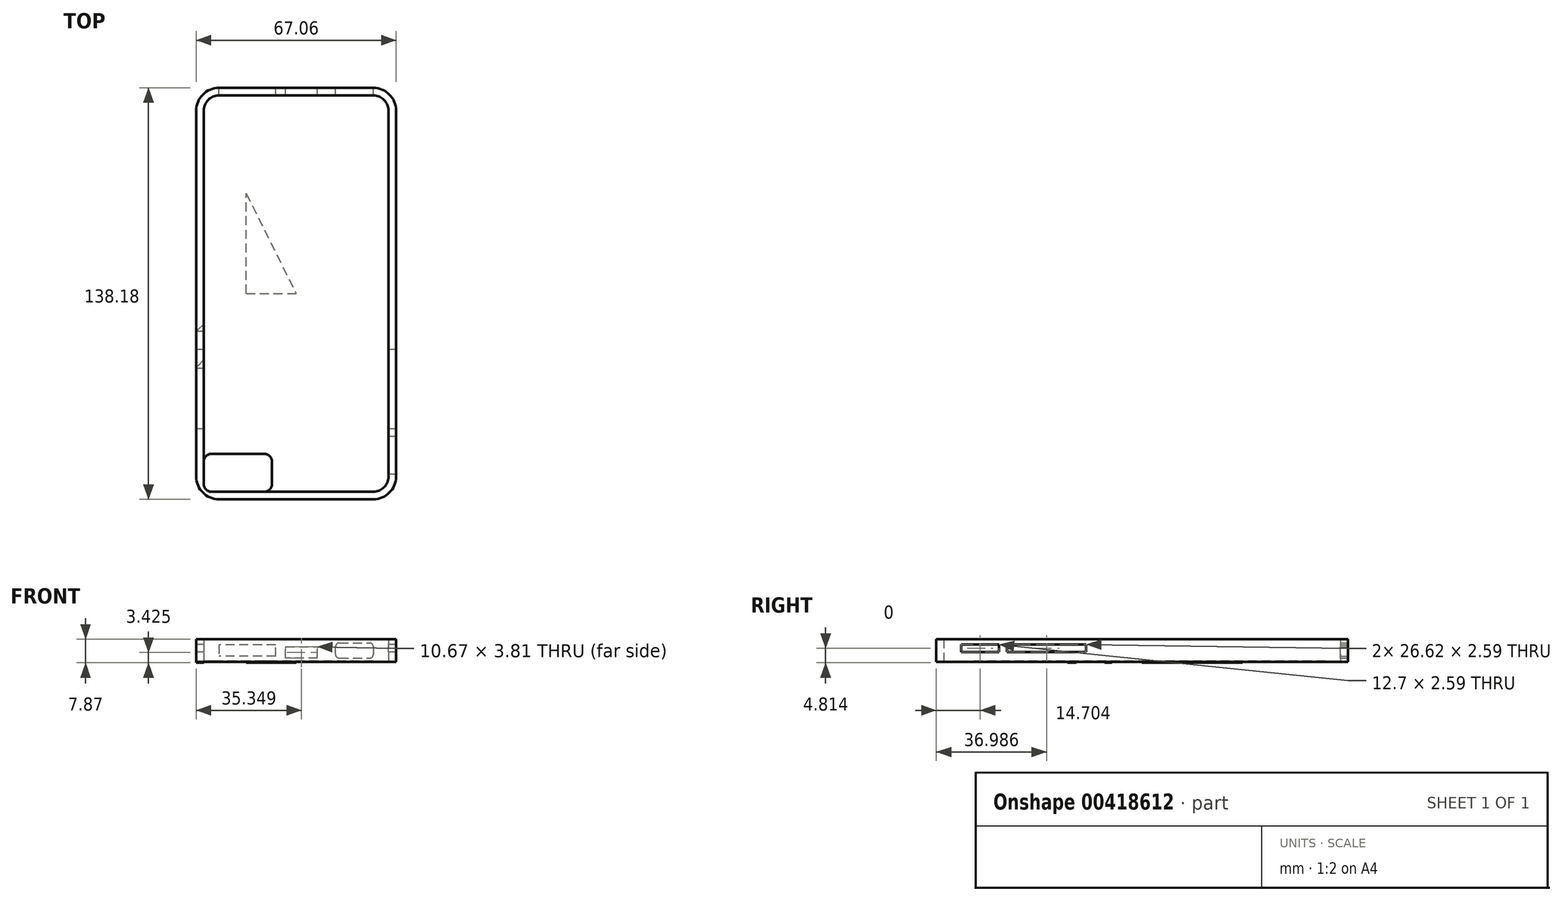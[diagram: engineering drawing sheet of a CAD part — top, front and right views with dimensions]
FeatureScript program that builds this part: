
annotation { "Feature Type Name" : "Feature", "Feature Type Description" : "" }
export const myFeature = defineFeature(function(context is Context, id is Id, definition is map)
    precondition{}
    {
        {
            var Q0;
            Q0=qCreatedBy(makeId("Top.planeOp"),FACE);
            var sketch = newSketch(context, id + "F0", { "sketchPlane" : qUnion([Q0])});
            skLineSegment(sketch, "E0", {"start": v(0, 0) * mm, "end": v(-33.53, 0) * mm});
            skLineSegment(sketch, "E1", {"start": v(-33.53, 0) * mm, "end": v(-33.53, 138.18) * mm});
            skLineSegment(sketch, "E2", {"start": v(-33.53, 138.18) * mm, "end": v(0, 138.18) * mm});
            skLineSegment(sketch, "E3", {"start": v(0, 138.18) * mm, "end": v(33.53, 138.18) * mm});
            skLineSegment(sketch, "E4", {"start": v(33.53, 138.18) * mm, "end": v(33.53, 0) * mm});
            skLineSegment(sketch, "E5", {"start": v(33.53, 0) * mm, "end": v(0, 0) * mm});
            skLineSegment(sketch, "E6", {"start": v(-30.99, 135.64) * mm, "end": v(-30.99, 2.54) * mm});
            skLineSegment(sketch, "E7", {"start": v(-30.99, 2.54) * mm, "end": v(30.99, 2.54) * mm});
            skLineSegment(sketch, "E8", {"start": v(30.99, 2.54) * mm, "end": v(30.99, 135.64) * mm});
            skLineSegment(sketch, "E9", {"start": v(30.99, 135.64) * mm, "end": v(-30.99, 135.64) * mm});
            skSolve(sketch);
        }
        {
            var Q0;
            Q0 = qSketchRegion(id + "F0", true);
            extrude(context, id + "F1", {"entities" : qUnion([Q0]), "depth" : 7.62 * mm});
        }
        {
            var Q0;
            Q0=makeQuery(id+"F0.imprint","IMPRINT",FACE,{"disambiguationData":[TD([[makeQuery(id+"F0.imprint","IMPRINT",EDGE,{"derivedFrom":sQuery(id+"F0.wireOp",EDGE,"E6")}),1.0]])]});
            extrude(context, id + "F2", {"entities" : qUnion([Q0]), "operationType" : NewBodyOperationType.ADD, "depth" : 0.25 * mm});
        }
        {
            var Q0;
            Q0=makeQuery(id+"F1.opExtrude","SWEPT_EDGE",EDGE,{"disambiguationData":[OSD([sQuery(id+"F0.wireOp",EDGE,"E0"),sQuery(id+"F0.wireOp",EDGE,"E1")])]});
            var Q1;
            Q1=makeQuery(id+"F1.opExtrude","SWEPT_EDGE",EDGE,{"disambiguationData":[OSD([sQuery(id+"F0.wireOp",EDGE,"E4"),sQuery(id+"F0.wireOp",EDGE,"E5")])]});
            var Q2;
            Q2=makeQuery(id+"F1.opExtrude","SWEPT_EDGE",EDGE,{"disambiguationData":[OSD([sQuery(id+"F0.wireOp",EDGE,"E3"),sQuery(id+"F0.wireOp",EDGE,"E4")])]});
            var Q3;
            Q3=makeQuery(id+"F1.opExtrude","SWEPT_EDGE",EDGE,{"disambiguationData":[OSD([sQuery(id+"F0.wireOp",EDGE,"E1"),sQuery(id+"F0.wireOp",EDGE,"E2")])]});
            fillet(context, id + "F3", {"entities" : qUnion([Q0, Q1, Q2, Q3]), "radius" : 7.62 * mm, "tangentPropagation" : true, "allowEdgeOverflow" : false});
        }
        {
            var Q0;
            Q0=makeQuery(id+"F1.opExtrude","SWEPT_EDGE",EDGE,{"disambiguationData":[OSD([sQuery(id+"F0.wireOp",EDGE,"E6"),sQuery(id+"F0.wireOp",EDGE,"E9")])]});
            var Q1;
            Q1=makeQuery(id+"F1.opExtrude","SWEPT_EDGE",EDGE,{"disambiguationData":[OSD([sQuery(id+"F0.wireOp",EDGE,"E8"),sQuery(id+"F0.wireOp",EDGE,"E9")])]});
            var Q2;
            Q2=makeQuery(id+"F1.opExtrude","SWEPT_EDGE",EDGE,{"disambiguationData":[OSD([sQuery(id+"F0.wireOp",EDGE,"E6"),sQuery(id+"F0.wireOp",EDGE,"E7")])]});
            var Q3;
            Q3=makeQuery(id+"F1.opExtrude","SWEPT_EDGE",EDGE,{"disambiguationData":[OSD([sQuery(id+"F0.wireOp",EDGE,"E7"),sQuery(id+"F0.wireOp",EDGE,"E8")])]});
            fillet(context, id + "F4", {"entities" : qUnion([Q0, Q1, Q2, Q3]), "radius" : 5.08 * mm, "tangentPropagation" : true, "allowEdgeOverflow" : false});
        }
        {
            var Q0;
            Q0=makeQuery(id+"F0.imprint","IMPRINT",FACE,{"disambiguationData":[TD([[makeQuery(id+"F0.imprint","IMPRINT",EDGE,{"derivedFrom":sQuery(id+"F0.wireOp",EDGE,"E6")}),1.0]])]});
            var sketch = newSketch(context, id + "F5", { "sketchPlane" : qUnion([Q0])});
            skLineSegment(sketch, "E10.0", {"start": v(-33.53, 138.18) * mm, "end": v(0, 138.18) * mm});
            skLineSegment(sketch, "E11.0", {"start": v(-33.53, 0) * mm, "end": v(-33.53, 138.18) * mm});
            skLineSegment(sketch, "E12.0", {"start": v(33.53, 138.18) * mm, "end": v(33.53, 0) * mm});
            skLineSegment(sketch, "E13.0", {"start": v(0, 0) * mm, "end": v(-33.53, 0) * mm});
            skLineSegment(sketch, "E14.0", {"start": v(33.53, 0) * mm, "end": v(0, 0) * mm});
            skPoint(sketch, "E15.start.orphan", {"position": v(-16.76, 138.18) * mm});
            skLineSegment(sketch, "E16", {"start": v(0, 138.18) * mm, "end": v(0, 69.09) * mm});
            skPoint(sketch, "E17.orphan", {"position": v(-33.53, 69.09) * mm});
            skPoint(sketch, "E18.end.orphan", {"position": v(33.53, 69.09) * mm});
            skLineSegment(sketch, "E19", {"start": v(-33.53, 69.09) * mm, "end": v(0, 69.09) * mm});
            skLineSegment(sketch, "E20", {"start": v(0, 69.09) * mm, "end": v(33.53, 69.09) * mm});
            skPoint(sketch, "E21", {"position": v(-16.76, 69.09) * mm});
            skLineSegment(sketch, "E22", {"start": v(-16.76, 69.09) * mm, "end": v(-16.76, 102.75) * mm});
            skLineSegment(sketch, "E23", {"start": v(-16.76, 102.75) * mm, "end": v(0, 69.09) * mm});
            skLineSegment(sketch, "E24", {"start": v(0, 69.09) * mm, "end": v(16.76, 69.09) * mm});
            skLineSegment(sketch, "E25", {"start": v(16.76, 69.09) * mm, "end": v(24.75, 61.14) * mm});
            skLineSegment(sketch, "E26", {"start": v(24.75, 61.14) * mm, "end": v(0, 61.14) * mm});
            skLineSegment(sketch, "E27", {"start": v(0, 61.14) * mm, "end": v(0, 52.13) * mm});
            skLineSegment(sketch, "E28", {"start": v(0, 52.13) * mm, "end": v(26.95, 52.13) * mm});
            skLineSegment(sketch, "E29", {"start": v(26.95, 52.13) * mm, "end": v(33.53, 44.08) * mm});
            skLineSegment(sketch, "E30", {"start": v(33.53, 44.08) * mm, "end": v(0, 44.08) * mm});
            skLineSegment(sketch, "E31", {"start": v(-16.76, 61.14) * mm, "end": v(-16.76, 69.09) * mm});
            skLineSegment(sketch, "E32", {"start": v(-16.76, 61.14) * mm, "end": v(-28.48, 61.14) * mm});
            skLineSegment(sketch, "E33", {"start": v(-28.48, 61.14) * mm, "end": v(-33.53, 56.5) * mm});
            skLineSegment(sketch, "E34", {"start": v(-33.53, 56.5) * mm, "end": v(-16.76, 56.5) * mm});
            skLineSegment(sketch, "E35", {"start": v(-16.76, 56.5) * mm, "end": v(-16.76, 52.13) * mm});
            skLineSegment(sketch, "E36", {"start": v(-16.76, 52.13) * mm, "end": v(-26.29, 52.13) * mm});
            skLineSegment(sketch, "E37", {"start": v(-26.29, 52.13) * mm, "end": v(-33.53, 44.08) * mm});
            skLineSegment(sketch, "E38", {"start": v(-33.53, 44.08) * mm, "end": v(0, 44.08) * mm});
            skSolve(sketch);
        }
        {
            var Q0;
            {var subQ14=sQuery(id+"F5.wireOp",EDGE,"E24");Q0=makeQuery(id+"F5.imprint","IMPRINT",FACE,{"disambiguationData":[TD([[makeQuery(id+"F5.imprint","IMPRINT",EDGE,{"derivedFrom":subQ14}),-1.0]])]});}
            var Q1;
            {var subQ1=sQuery(id+"F5.wireOp",EDGE,"E37");var subQ3=makeQuery(id+"F0.imprint","IMPRINT",EDGE,{"derivedFrom":sQuery(id+"F0.wireOp",EDGE,"E6")});var subQ4=makeQuery(id+"F5.imprint","INTERSECT",VERTEX,{"derivedFrom":[subQ3,subQ1]});Q1=makeQuery(id+"F5.imprint","IMPRINT",FACE,{"disambiguationData":[TD([[makeQuery(id+"F5.imprint","IMPRINT",EDGE,{"disambiguationData":[TD([[subQ4,-1.0]])],"derivedFrom":subQ3}),-1.0]])]});}
            var Q2;
            {var subQ1=sQuery(id+"F5.wireOp",EDGE,"E33");var subQ3=makeQuery(id+"F0.imprint","IMPRINT",EDGE,{"derivedFrom":sQuery(id+"F0.wireOp",EDGE,"E6")});var subQ4=makeQuery(id+"F5.imprint","INTERSECT",VERTEX,{"derivedFrom":[subQ3,subQ1]});Q2=makeQuery(id+"F5.imprint","IMPRINT",FACE,{"disambiguationData":[TD([[makeQuery(id+"F5.imprint","IMPRINT",EDGE,{"disambiguationData":[TD([[subQ4,-1.0]])],"derivedFrom":subQ3}),-1.0]])]});}
            var Q3;
            {var subQ2=sQuery(id+"F5.wireOp",EDGE,"E22");Q3=makeQuery(id+"F5.imprint","IMPRINT",FACE,{"disambiguationData":[TD([[makeQuery(id+"F5.imprint","IMPRINT",EDGE,{"derivedFrom":subQ2}),-1.0]])]});}
            extrude(context, id + "F6", {"entities" : qUnion([Q0, Q1, Q2, Q3]), "operationType" : NewBodyOperationType.ADD, "oppositeDirection" : true, "depth" : 0.25 * mm});
        }
        {
            var Q0;
            Q0=makeQuery(id+"F1.opExtrude","SWEPT_FACE",FACE,{"disambiguationData":[OSD([sQuery(id+"F0.wireOp",EDGE,"E1")])]});
            var sketch = newSketch(context, id + "F7", { "sketchPlane" : qUnion([Q0])});
            skLineSegment(sketch, "E39.0", {"start": v(0, 0) * mm, "end": v(-138.18, 0) * mm});
            skPoint(sketch, "E40", {"position": v(-50.3, 0) * mm});
            skLineSegment(sketch, "E41", {"start": v(-50.3, 0) * mm, "end": v(-23.68, 0) * mm});
            skLineSegment(sketch, "E42", {"start": v(-50.3, 0) * mm, "end": v(-50.3, 7.62) * mm});
            skLineSegment(sketch, "E43", {"start": v(-50.3, 5.86) * mm, "end": v(-50.3, 3.27) * mm});
            skLineSegment(sketch, "E44", {"start": v(-50.3, 3.27) * mm, "end": v(-23.68, 3.27) * mm});
            skLineSegment(sketch, "E45", {"start": v(-23.68, 3.27) * mm, "end": v(-23.68, 5.86) * mm});
            skLineSegment(sketch, "E46", {"start": v(-23.68, 5.86) * mm, "end": v(-50.3, 5.86) * mm});
            skLineSegment(sketch, "E47", {"start": v(-21.05, 3.27) * mm, "end": v(-21.05, 5.86) * mm});
            skLineSegment(sketch, "E48", {"start": v(-21.05, 5.86) * mm, "end": v(-21.05, 3.27) * mm});
            skLineSegment(sketch, "E49", {"start": v(-21.05, 3.27) * mm, "end": v(-8.36, 3.27) * mm});
            skLineSegment(sketch, "E50", {"start": v(-21.05, 5.86) * mm, "end": v(-8.36, 5.86) * mm});
            skLineSegment(sketch, "E51", {"start": v(-8.36, 5.86) * mm, "end": v(-8.36, 3.27) * mm});
            skSolve(sketch);
        }
        {
            var Q0;
            Q0 = qSketchRegion(id + "F7", true);
            extrude(context, id + "F8", {"entities" : qUnion([Q0]), "operationType" : NewBodyOperationType.REMOVE, "oppositeDirection" : true, "depth" : 381 * mm});
        }
        {
            var Q0;
            Q0=makeQuery(id+"F1.opExtrude","SWEPT_FACE",FACE,{"disambiguationData":[OSD([sQuery(id+"F0.wireOp",EDGE,"E1")])]});
            var sketch = newSketch(context, id + "F9", { "sketchPlane" : qUnion([Q0])});
            skLineSegment(sketch, "E52.0", {"start": v(-21.05, 3.27) * mm, "end": v(-8.36, 3.27) * mm});
            skLineSegment(sketch, "E53.0", {"start": v(-21.05, 5.86) * mm, "end": v(-21.05, 3.27) * mm});
            skLineSegment(sketch, "E54.0", {"start": v(-21.05, 5.86) * mm, "end": v(-8.36, 5.86) * mm});
            skLineSegment(sketch, "E55.0", {"start": v(-8.36, 5.86) * mm, "end": v(-8.36, 3.27) * mm});
            skSolve(sketch);
        }
        {
            var Q0;
            Q0 = qSketchRegion(id + "F9", true);
            extrude(context, id + "F10", {"entities" : qUnion([Q0]), "operationType" : NewBodyOperationType.ADD, "oppositeDirection" : true, "depth" : 2.54 * mm});
        }
        {
            var Q0;
            Q0=makeQuery(id+"F10.boolean.opBoolean","MERGE",FACE,{"derivedFrom":[makeQuery(id+"F1.opExtrude","SWEPT_FACE",FACE,{"disambiguationData":[OSD([sQuery(id+"F0.wireOp",EDGE,"E1")])]}),makeQuery(id+"F10.opExtrude","CAP_FACE",FACE,{"disambiguationData":[OSD([sQuery(id+"F9.wireOp",EDGE,"E52.0"),sQuery(id+"F9.wireOp",EDGE,"E53.0"),sQuery(id+"F9.wireOp",EDGE,"E54.0"),sQuery(id+"F9.wireOp",EDGE,"E55.0")])],"isStart":true})]});
            var sketch = newSketch(context, id + "F11", { "sketchPlane" : qUnion([Q0])});
            skLineSegment(sketch, "E56.0", {"start": v(-23.68, 5.86) * mm, "end": v(-50.3, 5.86) * mm});
            skLineSegment(sketch, "E57.0", {"start": v(-23.68, 3.27) * mm, "end": v(-23.68, 5.86) * mm});
            skLineSegment(sketch, "E58.0", {"start": v(-50.3, 3.27) * mm, "end": v(-23.68, 3.27) * mm});
            skLineSegment(sketch, "E59.0", {"start": v(-50.3, 5.86) * mm, "end": v(-50.3, 3.27) * mm});
            skLineSegment(sketch, "E60", {"start": v(-36.99, 5.86) * mm, "end": v(-36.99, 3.27) * mm});
            skLineSegment(sketch, "E61.0", {"start": v(0, 0) * mm, "end": v(-138.18, 0) * mm});
            skSolve(sketch);
        }
        {
            var Q0;
            {var subQ0=sQuery(id+"F11.wireOp",EDGE,"E59.0");Q0=makeQuery(id+"F11.imprint","IMPRINT",FACE,{"disambiguationData":[TD([[makeQuery(id+"F11.imprint","IMPRINT",EDGE,{"derivedFrom":subQ0}),1.0]])]});}
            extrude(context, id + "F12", {"entities" : qUnion([Q0]), "operationType" : NewBodyOperationType.ADD, "oppositeDirection" : true, "depth" : 2.54 * mm});
        }
        {
            var Q0;
            Q0=makeQuery(id+"F0.imprint","IMPRINT",FACE,{"disambiguationData":[TD([[makeQuery(id+"F0.imprint","IMPRINT",EDGE,{"derivedFrom":sQuery(id+"F0.wireOp",EDGE,"E6")}),1.0]])]});
            var sketch = newSketch(context, id + "F13", { "sketchPlane" : qUnion([Q0])});
            skLineSegment(sketch, "E62.0", {"start": v(-33.53, 0) * mm, "end": v(-33.53, 138.18) * mm});
            skPoint(sketch, "E63", {"position": v(-33.53, 15.24) * mm});
            skLineSegment(sketch, "E64.0", {"start": v(-30.99, 135.64) * mm, "end": v(-30.99, 2.54) * mm});
            skLineSegment(sketch, "E65", {"start": v(-33.53, 15.24) * mm, "end": v(-30.99, 15.24) * mm});
            skLineSegment(sketch, "E66", {"start": v(-30.99, 15.24) * mm, "end": v(-8.13, 15.24) * mm});
            skLineSegment(sketch, "E67", {"start": v(-8.13, 15.24) * mm, "end": v(-8.13, 2.54) * mm});
            skLineSegment(sketch, "E68", {"start": v(-30.99, 2.54) * mm, "end": v(-8.13, 2.54) * mm});
            skSolve(sketch);
        }
        {
            var Q0;
            Q0 = qSketchRegion(id + "F13", true);
            extrude(context, id + "F14", {"entities" : qUnion([Q0]), "operationType" : NewBodyOperationType.REMOVE, "depth" : 25.4 * mm});
        }
        {
            var Q0;
            Q0=makeQuery(id+"F14.boolean.opBoolean","COPY",EDGE,{"derivedFrom":makeQuery(id+"F14.opExtrude","SWEPT_EDGE",EDGE,{"disambiguationData":[OSD([sQuery(id+"F13.wireOp",EDGE,"E66"),sQuery(id+"F13.wireOp",EDGE,"E67")])]})});
            var Q1;
            Q1=makeQuery(id+"F14.boolean.opBoolean","COPY",EDGE,{"derivedFrom":makeQuery(id+"F14.opExtrude","SWEPT_EDGE",EDGE,{"disambiguationData":[OSD([sQuery(id+"F0.wireOp",EDGE,"E7"),sQuery(id+"F13.wireOp",EDGE,"E67"),sQuery(id+"F13.wireOp",EDGE,"E68")])]})});
            var Q2;
            Q2=makeQuery(id+"F14.boolean.opBoolean","COPY",EDGE,{"derivedFrom":makeQuery(id+"F14.opExtrude","SWEPT_EDGE",EDGE,{"disambiguationData":[OSD([sQuery(id+"F13.wireOp",EDGE,"E64.0"),sQuery(id+"F13.wireOp",EDGE,"E68")])]})});
            var Q3;
            Q3=makeQuery(id+"F14.boolean.opBoolean","COPY",EDGE,{"derivedFrom":makeQuery(id+"F14.opExtrude","SWEPT_EDGE",EDGE,{"disambiguationData":[OSD([sQuery(id+"F13.wireOp",EDGE,"E64.0"),sQuery(id+"F13.wireOp",EDGE,"E66")])]})});
            fillet(context, id + "F15", {"entities" : qUnion([Q0, Q1, Q2, Q3]), "radius" : 2.54 * mm, "tangentPropagation" : true, "allowEdgeOverflow" : false});
        }
        {
            var Q0;
            Q0=makeQuery(id+"F1.opExtrude","SWEPT_FACE",FACE,{"disambiguationData":[OSD([sQuery(id+"F0.wireOp",EDGE,"E2"),sQuery(id+"F0.wireOp",EDGE,"E3")])]});
            var sketch = newSketch(context, id + "F16", { "sketchPlane" : qUnion([Q0])});
            skLineSegment(sketch, "E69", {"start": v(-25.9, 6.35) * mm, "end": v(-13.2, 6.35) * mm});
            skLineSegment(sketch, "E70", {"start": v(-25.9, 1.27) * mm, "end": v(-13.2, 1.27) * mm});
            skLineSegment(sketch, "E71", {"start": v(-25.9, 3.81) * mm, "end": v(-13.2, 3.81) * mm, "construction": true});
            skLineSegment(sketch, "E72", {"start": v(-13.2, 6.35) * mm, "end": v(-13.2, 1.27) * mm});
            skSolve(sketch);
        }
        {
            var Q0;
            {var subQ0=sQuery(id+"F16.wireOp",EDGE,"E69");Q0=makeQuery(id+"F16.imprint","IMPRINT",FACE,{"disambiguationData":[TD([[makeQuery(id+"F16.imprint","IMPRINT",EDGE,{"derivedFrom":subQ0}),-1.0]])]});}
            extrude(context, id + "F17", {"entities" : qUnion([Q0]), "operationType" : NewBodyOperationType.REMOVE, "oppositeDirection" : true, "depth" : 25.4 * mm});
        }
        {
            var Q0;
            Q0=makeQuery(id+"F17.boolean.opBoolean","COPY",EDGE,{"derivedFrom":makeQuery(id+"F17.opExtrude","SWEPT_EDGE",EDGE,{"disambiguationData":[OSD([sQuery(id+"F16.wireOp",EDGE,"E70"),sQuery(id+"F16.wireOp",EDGE,"E72")])]})});
            var Q1;
            Q1=makeQuery(id+"F17.boolean.opBoolean","COPY",EDGE,{"derivedFrom":makeQuery(id+"F17.opExtrude","SWEPT_EDGE",EDGE,{"disambiguationData":[OSD([sQuery(id+"F0.wireOp",EDGE,"E2"),sQuery(id+"F0.wireOp",EDGE,"E3"),sQuery(id+"F0.wireOp",EDGE,"E4"),sQuery(id+"F16.wireOp",EDGE,"E70")])]})});
            var Q2;
            Q2=makeQuery(id+"F17.boolean.opBoolean","COPY",EDGE,{"derivedFrom":makeQuery(id+"F17.opExtrude","SWEPT_EDGE",EDGE,{"disambiguationData":[OSD([sQuery(id+"F0.wireOp",EDGE,"E2"),sQuery(id+"F0.wireOp",EDGE,"E3"),sQuery(id+"F0.wireOp",EDGE,"E4"),sQuery(id+"F16.wireOp",EDGE,"E69")])]})});
            var Q3;
            Q3=makeQuery(id+"F17.boolean.opBoolean","COPY",EDGE,{"derivedFrom":makeQuery(id+"F17.opExtrude","SWEPT_EDGE",EDGE,{"disambiguationData":[OSD([sQuery(id+"F16.wireOp",EDGE,"E69"),sQuery(id+"F16.wireOp",EDGE,"E72")])]})});
            fillet(context, id + "F18", {"entities" : qUnion([Q0, Q1, Q2, Q3]), "radius" : 1.27 * mm, "tangentPropagation" : true, "allowEdgeOverflow" : false});
        }
        {
            var Q0;
            Q0=makeQuery(id+"F1.opExtrude","SWEPT_FACE",FACE,{"disambiguationData":[OSD([sQuery(id+"F0.wireOp",EDGE,"E2"),sQuery(id+"F0.wireOp",EDGE,"E3")])]});
            var sketch = newSketch(context, id + "F19", { "sketchPlane" : qUnion([Q0])});
            skLineSegment(sketch, "E73", {"start": v(25.9, 1.9) * mm, "end": v(6.86, 1.9) * mm});
            skLineSegment(sketch, "E74", {"start": v(25.9, 5.71) * mm, "end": v(6.86, 5.71) * mm});
            skLineSegment(sketch, "E75", {"start": v(25.9, 3.81) * mm, "end": v(6.86, 3.81) * mm, "construction": true});
            skLineSegment(sketch, "E76", {"start": v(6.86, 5.71) * mm, "end": v(6.86, 1.9) * mm});
            skSolve(sketch);
        }
        {
            var Q0;
            {var subQ0=sQuery(id+"F19.wireOp",EDGE,"E73");Q0=makeQuery(id+"F19.imprint","IMPRINT",FACE,{"disambiguationData":[TD([[makeQuery(id+"F19.imprint","IMPRINT",EDGE,{"derivedFrom":subQ0}),-1.0]])]});}
            extrude(context, id + "F20", {"entities" : qUnion([Q0]), "operationType" : NewBodyOperationType.REMOVE, "oppositeDirection" : true, "depth" : 25.4 * mm});
        }
        {
            var Q0;
            Q0=makeQuery(id+"F1.opExtrude","SWEPT_FACE",FACE,{"disambiguationData":[OSD([sQuery(id+"F0.wireOp",EDGE,"E2"),sQuery(id+"F0.wireOp",EDGE,"E3")])]});
            var sketch = newSketch(context, id + "F21", { "sketchPlane" : qUnion([Q0])});
            skLineSegment(sketch, "E77", {"start": v(-7.15, 5.08) * mm, "end": v(3.51, 5.08) * mm});
            skLineSegment(sketch, "E78", {"start": v(3.51, 5.08) * mm, "end": v(3.51, 1.27) * mm});
            skLineSegment(sketch, "E79", {"start": v(3.51, 1.27) * mm, "end": v(-7.15, 1.27) * mm});
            skLineSegment(sketch, "E80", {"start": v(3.51, 3.18) * mm, "end": v(-7.15, 3.18) * mm, "construction": true});
            skPoint(sketch, "E81.start.orphan", {"position": v(-13.58, 1.64) * mm});
            skLineSegment(sketch, "E82", {"start": v(-7.15, 5.08) * mm, "end": v(-7.15, 1.27) * mm});
            skSolve(sketch);
        }
        {
            var Q0;
            Q0 = qSketchRegion(id + "F21", true);
            extrude(context, id + "F22", {"entities" : qUnion([Q0]), "operationType" : NewBodyOperationType.REMOVE, "oppositeDirection" : true, "depth" : 25.4 * mm});
        }
    });
